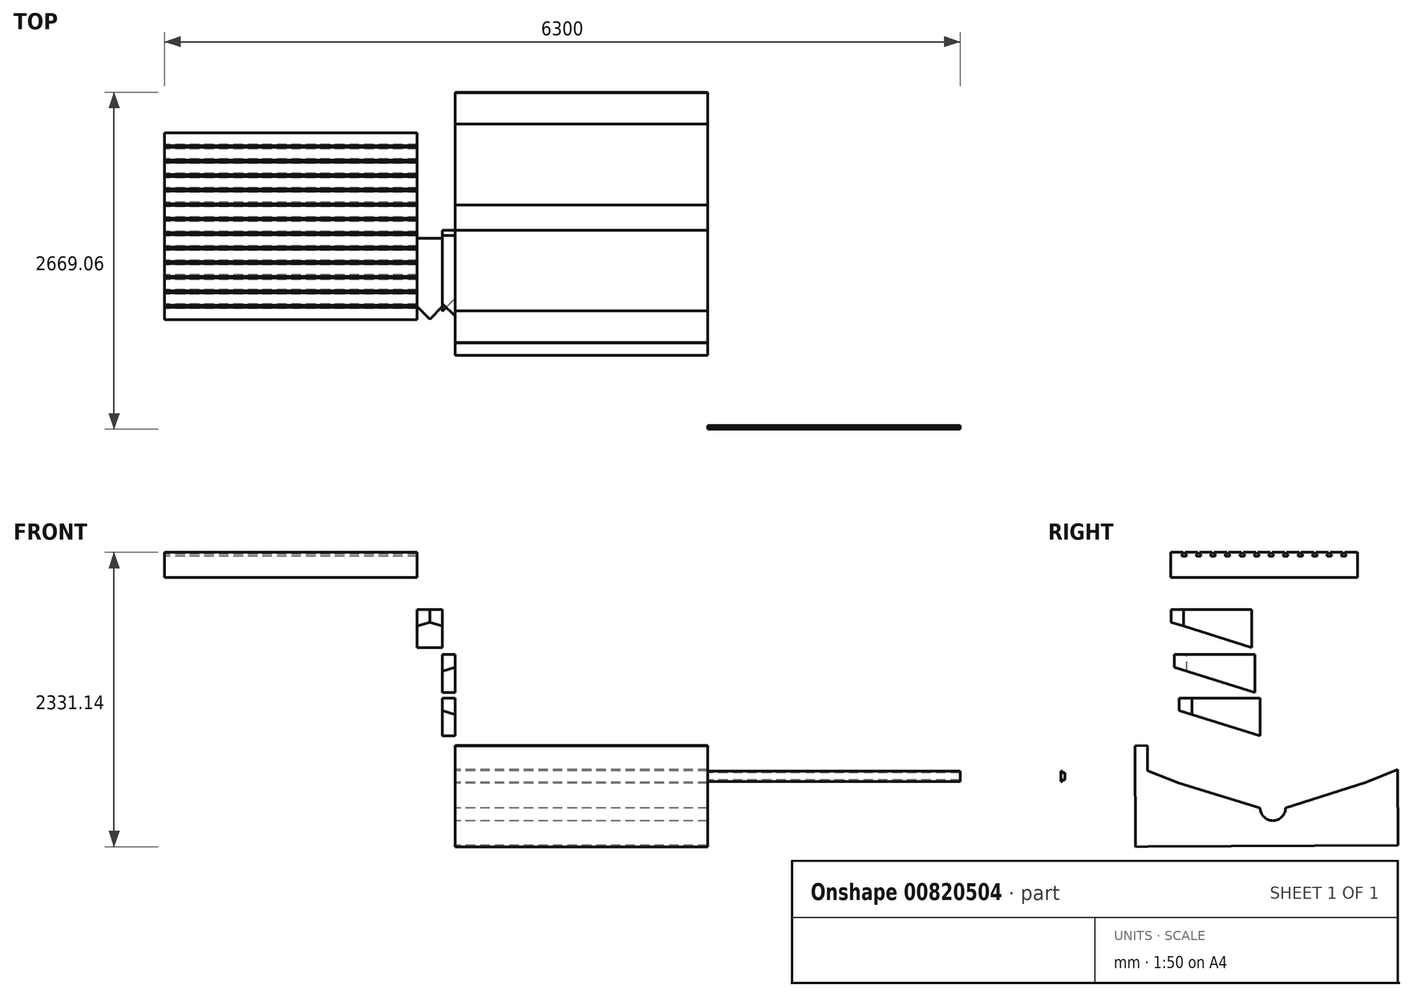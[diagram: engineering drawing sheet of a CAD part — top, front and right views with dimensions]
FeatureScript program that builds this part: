
annotation { "Feature Type Name" : "Feature", "Feature Type Description" : "" }
export const myFeature = defineFeature(function(context is Context, id is Id, definition is map)
    precondition{}
    {
        {
            var Q0;
            Q0=qCreatedBy(makeId("Right.planeOp"),FACE);
            var sketch = newSketch(context, id + "F0", { "sketchPlane" : qUnion([Q0])});
            skLineSegment(sketch, "E0", {"start": v(-68.68, 15) * mm, "end": v(31.32, 15) * mm});
            skLineSegment(sketch, "E1", {"start": v(31.32, 15) * mm, "end": v(31.32, 0) * mm});
            skLineSegment(sketch, "E2", {"start": v(31.32, 0) * mm, "end": v(21.32, 0) * mm});
            skLineSegment(sketch, "E3", {"start": v(21.32, 0) * mm, "end": v(21.32, -15) * mm});
            skLineSegment(sketch, "E4", {"start": v(21.32, -15) * mm, "end": v(56.32, -15) * mm});
            skLineSegment(sketch, "E5", {"start": v(56.32, -15) * mm, "end": v(56.32, 0) * mm});
            skLineSegment(sketch, "E6", {"start": v(56.32, 0) * mm, "end": v(46.32, 0) * mm});
            skLineSegment(sketch, "E7", {"start": v(46.32, 0) * mm, "end": v(46.32, 15) * mm});
            skLineSegment(sketch, "E8", {"start": v(46.32, 15) * mm, "end": v(146.32, 15) * mm});
            skLineSegment(sketch, "E9", {"start": v(146.32, 15) * mm, "end": v(146.32, 0) * mm});
            skLineSegment(sketch, "E10", {"start": v(146.32, 0) * mm, "end": v(136.32, 0) * mm});
            skLineSegment(sketch, "E11", {"start": v(136.32, 0) * mm, "end": v(136.32, -15) * mm});
            skLineSegment(sketch, "E12", {"start": v(136.32, -15) * mm, "end": v(171.32, -15) * mm});
            skLineSegment(sketch, "E13", {"start": v(171.32, -15) * mm, "end": v(171.32, 0) * mm});
            skLineSegment(sketch, "E14", {"start": v(171.32, 0) * mm, "end": v(161.32, 0) * mm});
            skLineSegment(sketch, "E15", {"start": v(161.32, 0) * mm, "end": v(161.32, 15) * mm});
            skLineSegment(sketch, "E16", {"start": v(161.32, 15) * mm, "end": v(261.32, 15) * mm});
            skLineSegment(sketch, "E17", {"start": v(261.32, 15) * mm, "end": v(261.32, 0) * mm});
            skLineSegment(sketch, "E18", {"start": v(261.32, 0) * mm, "end": v(251.32, 0) * mm});
            skLineSegment(sketch, "E19", {"start": v(251.32, 0) * mm, "end": v(251.32, -15) * mm});
            skLineSegment(sketch, "E20", {"start": v(251.32, -15) * mm, "end": v(286.32, -15) * mm});
            skLineSegment(sketch, "E21", {"start": v(286.32, -15) * mm, "end": v(286.32, 0) * mm});
            skLineSegment(sketch, "E22", {"start": v(286.32, 0) * mm, "end": v(276.32, 0) * mm});
            skLineSegment(sketch, "E23", {"start": v(276.32, 0) * mm, "end": v(276.32, 15) * mm});
            skLineSegment(sketch, "E24", {"start": v(276.32, 15) * mm, "end": v(376.32, 15) * mm});
            skLineSegment(sketch, "E25", {"start": v(376.32, 15) * mm, "end": v(376.32, 0) * mm});
            skLineSegment(sketch, "E26", {"start": v(376.32, 0) * mm, "end": v(366.32, 0) * mm});
            skLineSegment(sketch, "E27", {"start": v(366.32, 0) * mm, "end": v(366.32, -15) * mm});
            skLineSegment(sketch, "E28", {"start": v(366.32, -15) * mm, "end": v(401.32, -15) * mm});
            skLineSegment(sketch, "E29", {"start": v(401.32, -15) * mm, "end": v(401.32, 0) * mm});
            skLineSegment(sketch, "E30", {"start": v(401.32, 0) * mm, "end": v(391.32, 0) * mm});
            skLineSegment(sketch, "E31", {"start": v(391.32, 0) * mm, "end": v(391.32, 15) * mm});
            skLineSegment(sketch, "E32", {"start": v(391.32, 15) * mm, "end": v(491.32, 15) * mm});
            skLineSegment(sketch, "E33", {"start": v(491.32, 15) * mm, "end": v(491.32, 0) * mm});
            skLineSegment(sketch, "E34", {"start": v(491.32, 0) * mm, "end": v(481.32, 0) * mm});
            skLineSegment(sketch, "E35", {"start": v(481.32, 0) * mm, "end": v(481.32, -15) * mm});
            skLineSegment(sketch, "E36", {"start": v(481.32, -15) * mm, "end": v(516.32, -15) * mm});
            skLineSegment(sketch, "E37", {"start": v(516.32, -15) * mm, "end": v(516.32, 0) * mm});
            skLineSegment(sketch, "E38", {"start": v(516.32, 0) * mm, "end": v(506.32, 0) * mm});
            skLineSegment(sketch, "E39", {"start": v(506.32, 0) * mm, "end": v(506.32, 15) * mm});
            skLineSegment(sketch, "E40", {"start": v(506.32, 15) * mm, "end": v(606.32, 15) * mm});
            skLineSegment(sketch, "E41", {"start": v(606.32, 15) * mm, "end": v(606.32, 0) * mm});
            skLineSegment(sketch, "E42", {"start": v(606.32, 0) * mm, "end": v(596.32, 0) * mm});
            skLineSegment(sketch, "E43", {"start": v(596.32, 0) * mm, "end": v(596.32, -15) * mm});
            skLineSegment(sketch, "E44", {"start": v(596.32, -15) * mm, "end": v(631.32, -15) * mm});
            skLineSegment(sketch, "E45", {"start": v(631.32, -15) * mm, "end": v(631.32, 0) * mm});
            skLineSegment(sketch, "E46", {"start": v(631.32, 0) * mm, "end": v(621.32, 0) * mm});
            skLineSegment(sketch, "E47", {"start": v(621.32, 0) * mm, "end": v(621.32, 15) * mm});
            skLineSegment(sketch, "E48", {"start": v(621.32, 15) * mm, "end": v(721.32, 15) * mm});
            skLineSegment(sketch, "E49", {"start": v(721.32, 15) * mm, "end": v(721.32, 0) * mm});
            skLineSegment(sketch, "E50", {"start": v(721.32, 0) * mm, "end": v(711.32, 0) * mm});
            skLineSegment(sketch, "E51", {"start": v(711.32, 0) * mm, "end": v(711.32, -15) * mm});
            skLineSegment(sketch, "E52", {"start": v(711.32, -15) * mm, "end": v(746.32, -15) * mm});
            skLineSegment(sketch, "E53", {"start": v(746.32, -15) * mm, "end": v(746.32, 0) * mm});
            skLineSegment(sketch, "E54", {"start": v(746.32, 0) * mm, "end": v(736.32, 0) * mm});
            skLineSegment(sketch, "E55", {"start": v(736.32, 0) * mm, "end": v(736.32, 15) * mm});
            skLineSegment(sketch, "E56", {"start": v(736.32, 15) * mm, "end": v(836.32, 15) * mm});
            skLineSegment(sketch, "E57", {"start": v(836.32, 15) * mm, "end": v(836.32, 0) * mm});
            skLineSegment(sketch, "E58", {"start": v(836.32, 0) * mm, "end": v(826.32, 0) * mm});
            skLineSegment(sketch, "E59", {"start": v(826.32, 0) * mm, "end": v(826.32, -15) * mm});
            skLineSegment(sketch, "E60", {"start": v(826.32, -15) * mm, "end": v(861.32, -15) * mm});
            skLineSegment(sketch, "E61", {"start": v(861.32, -15) * mm, "end": v(861.32, 0) * mm});
            skLineSegment(sketch, "E62", {"start": v(861.32, 0) * mm, "end": v(851.32, 0) * mm});
            skLineSegment(sketch, "E63", {"start": v(851.32, 0) * mm, "end": v(851.32, 15) * mm});
            skLineSegment(sketch, "E64", {"start": v(851.32, 15) * mm, "end": v(951.32, 15) * mm});
            skLineSegment(sketch, "E65", {"start": v(951.32, 15) * mm, "end": v(951.32, 0) * mm});
            skLineSegment(sketch, "E66", {"start": v(951.32, 0) * mm, "end": v(941.32, 0) * mm});
            skLineSegment(sketch, "E67", {"start": v(941.32, 0) * mm, "end": v(941.32, -15) * mm});
            skLineSegment(sketch, "E68", {"start": v(941.32, -15) * mm, "end": v(976.32, -15) * mm});
            skLineSegment(sketch, "E69", {"start": v(976.32, -15) * mm, "end": v(976.32, 0) * mm});
            skLineSegment(sketch, "E70", {"start": v(976.32, 0) * mm, "end": v(966.32, 0) * mm});
            skLineSegment(sketch, "E71", {"start": v(966.32, 0) * mm, "end": v(966.32, 15) * mm});
            skLineSegment(sketch, "E72", {"start": v(966.32, 15) * mm, "end": v(1066.32, 15) * mm});
            skLineSegment(sketch, "E73", {"start": v(1066.32, 15) * mm, "end": v(1066.32, 0) * mm});
            skLineSegment(sketch, "E74", {"start": v(1066.32, 0) * mm, "end": v(1056.32, 0) * mm});
            skLineSegment(sketch, "E75", {"start": v(1056.32, 0) * mm, "end": v(1056.32, -15) * mm});
            skLineSegment(sketch, "E76", {"start": v(1056.32, -15) * mm, "end": v(1091.32, -15) * mm});
            skLineSegment(sketch, "E77", {"start": v(1091.32, -15) * mm, "end": v(1091.32, 0) * mm});
            skLineSegment(sketch, "E78", {"start": v(1091.32, 0) * mm, "end": v(1081.32, 0) * mm});
            skLineSegment(sketch, "E79", {"start": v(1081.32, 0) * mm, "end": v(1081.32, 15) * mm});
            skLineSegment(sketch, "E80", {"start": v(1081.32, 15) * mm, "end": v(1181.32, 15) * mm});
            skLineSegment(sketch, "E81", {"start": v(1181.32, 15) * mm, "end": v(1181.32, 0) * mm});
            skLineSegment(sketch, "E82", {"start": v(1181.32, 0) * mm, "end": v(1171.32, 0) * mm});
            skLineSegment(sketch, "E83", {"start": v(1171.32, 0) * mm, "end": v(1171.32, -15) * mm});
            skLineSegment(sketch, "E84", {"start": v(1171.32, -15) * mm, "end": v(1206.32, -15) * mm});
            skLineSegment(sketch, "E85", {"start": v(1206.32, -15) * mm, "end": v(1206.32, 0) * mm});
            skLineSegment(sketch, "E86", {"start": v(1206.32, 0) * mm, "end": v(1196.32, 0) * mm});
            skLineSegment(sketch, "E87", {"start": v(1196.32, 0) * mm, "end": v(1196.32, 15) * mm});
            skLineSegment(sketch, "E88", {"start": v(1196.32, 15) * mm, "end": v(1296.32, 15) * mm});
            skPoint(sketch, "E88.endSnap0", {"position": v(1131.32, 15) * mm});
            skLineSegment(sketch, "E89", {"start": v(1296.32, 15) * mm, "end": v(1296.32, 0) * mm});
            skLineSegment(sketch, "E90", {"start": v(1296.32, 0) * mm, "end": v(1286.32, 0) * mm});
            skLineSegment(sketch, "E91", {"start": v(1286.32, 0) * mm, "end": v(1286.32, -15) * mm});
            skLineSegment(sketch, "E92", {"start": v(1286.32, -15) * mm, "end": v(1321.32, -15) * mm});
            skLineSegment(sketch, "E93", {"start": v(1321.32, -15) * mm, "end": v(1321.32, 0) * mm});
            skLineSegment(sketch, "E94", {"start": v(1321.32, 0) * mm, "end": v(1311.32, 0) * mm});
            skLineSegment(sketch, "E95", {"start": v(1311.32, 0) * mm, "end": v(1311.32, 15) * mm});
            skLineSegment(sketch, "E96", {"start": v(1311.32, 15) * mm, "end": v(1411.32, 15) * mm});
            skLineSegment(sketch, "E97", {"start": v(1411.32, 15) * mm, "end": v(1411.32, -185) * mm});
            skLineSegment(sketch, "E98", {"start": v(1411.32, -185) * mm, "end": v(-68.68, -185) * mm});
            skLineSegment(sketch, "E99", {"start": v(-68.68, -185) * mm, "end": v(-68.68, 15) * mm});
            skSolve(sketch);
        }
        {
            var Q0;
            Q0=makeQuery(id+"F0.imprint","IMPRINT",FACE,{"disambiguationData":[TD([[makeQuery(id+"F0.imprint","IMPRINT",EDGE,{"derivedFrom":sQuery(id+"F0.wireOp",EDGE,"E0")}),-1.0]])]});
            extrude(context, id + "F1", {"entities" : qUnion([Q0]), "depth" : 2000 * mm, "offsetDistance" : 25 * mm});
        }
        {
            var Q0;
            Q0=makeQuery(id+"F1.opExtrude","CAP_FACE",FACE,{"disambiguationData":[OSD([sQuery(id+"F0.wireOp",EDGE,"E0"),sQuery(id+"F0.wireOp",EDGE,"E1"),sQuery(id+"F0.wireOp",EDGE,"E2"),sQuery(id+"F0.wireOp",EDGE,"E3"),sQuery(id+"F0.wireOp",EDGE,"E4"),sQuery(id+"F0.wireOp",EDGE,"E5"),sQuery(id+"F0.wireOp",EDGE,"E6"),sQuery(id+"F0.wireOp",EDGE,"E7"),sQuery(id+"F0.wireOp",EDGE,"E8"),sQuery(id+"F0.wireOp",EDGE,"E9"),sQuery(id+"F0.wireOp",EDGE,"E10"),sQuery(id+"F0.wireOp",EDGE,"E11"),sQuery(id+"F0.wireOp",EDGE,"E12"),sQuery(id+"F0.wireOp",EDGE,"E13"),sQuery(id+"F0.wireOp",EDGE,"E14"),sQuery(id+"F0.wireOp",EDGE,"E15"),sQuery(id+"F0.wireOp",EDGE,"E16"),sQuery(id+"F0.wireOp",EDGE,"E17"),sQuery(id+"F0.wireOp",EDGE,"E18"),sQuery(id+"F0.wireOp",EDGE,"E19"),sQuery(id+"F0.wireOp",EDGE,"E20"),sQuery(id+"F0.wireOp",EDGE,"E21"),sQuery(id+"F0.wireOp",EDGE,"E22"),sQuery(id+"F0.wireOp",EDGE,"E23"),sQuery(id+"F0.wireOp",EDGE,"E24"),sQuery(id+"F0.wireOp",EDGE,"E25"),sQuery(id+"F0.wireOp",EDGE,"E26"),sQuery(id+"F0.wireOp",EDGE,"E27"),sQuery(id+"F0.wireOp",EDGE,"E28"),sQuery(id+"F0.wireOp",EDGE,"E29"),sQuery(id+"F0.wireOp",EDGE,"E30"),sQuery(id+"F0.wireOp",EDGE,"E31"),sQuery(id+"F0.wireOp",EDGE,"E32"),sQuery(id+"F0.wireOp",EDGE,"E33"),sQuery(id+"F0.wireOp",EDGE,"E34"),sQuery(id+"F0.wireOp",EDGE,"E35"),sQuery(id+"F0.wireOp",EDGE,"E36"),sQuery(id+"F0.wireOp",EDGE,"E37"),sQuery(id+"F0.wireOp",EDGE,"E38"),sQuery(id+"F0.wireOp",EDGE,"E39"),sQuery(id+"F0.wireOp",EDGE,"E40"),sQuery(id+"F0.wireOp",EDGE,"E41"),sQuery(id+"F0.wireOp",EDGE,"E42"),sQuery(id+"F0.wireOp",EDGE,"E43"),sQuery(id+"F0.wireOp",EDGE,"E44"),sQuery(id+"F0.wireOp",EDGE,"E45"),sQuery(id+"F0.wireOp",EDGE,"E46"),sQuery(id+"F0.wireOp",EDGE,"E47"),sQuery(id+"F0.wireOp",EDGE,"E48"),sQuery(id+"F0.wireOp",EDGE,"E49"),sQuery(id+"F0.wireOp",EDGE,"E50"),sQuery(id+"F0.wireOp",EDGE,"E51"),sQuery(id+"F0.wireOp",EDGE,"E52"),sQuery(id+"F0.wireOp",EDGE,"E53"),sQuery(id+"F0.wireOp",EDGE,"E54"),sQuery(id+"F0.wireOp",EDGE,"E55"),sQuery(id+"F0.wireOp",EDGE,"E56"),sQuery(id+"F0.wireOp",EDGE,"E57"),sQuery(id+"F0.wireOp",EDGE,"E58"),sQuery(id+"F0.wireOp",EDGE,"E59"),sQuery(id+"F0.wireOp",EDGE,"E60"),sQuery(id+"F0.wireOp",EDGE,"E61"),sQuery(id+"F0.wireOp",EDGE,"E62"),sQuery(id+"F0.wireOp",EDGE,"E63"),sQuery(id+"F0.wireOp",EDGE,"E64"),sQuery(id+"F0.wireOp",EDGE,"E65"),sQuery(id+"F0.wireOp",EDGE,"E66"),sQuery(id+"F0.wireOp",EDGE,"E67"),sQuery(id+"F0.wireOp",EDGE,"E68"),sQuery(id+"F0.wireOp",EDGE,"E69"),sQuery(id+"F0.wireOp",EDGE,"E70"),sQuery(id+"F0.wireOp",EDGE,"E71"),sQuery(id+"F0.wireOp",EDGE,"E72"),sQuery(id+"F0.wireOp",EDGE,"E73"),sQuery(id+"F0.wireOp",EDGE,"E74"),sQuery(id+"F0.wireOp",EDGE,"E75"),sQuery(id+"F0.wireOp",EDGE,"E76"),sQuery(id+"F0.wireOp",EDGE,"E77"),sQuery(id+"F0.wireOp",EDGE,"E78"),sQuery(id+"F0.wireOp",EDGE,"E79"),sQuery(id+"F0.wireOp",EDGE,"E80"),sQuery(id+"F0.wireOp",EDGE,"E81"),sQuery(id+"F0.wireOp",EDGE,"E82"),sQuery(id+"F0.wireOp",EDGE,"E83"),sQuery(id+"F0.wireOp",EDGE,"E84"),sQuery(id+"F0.wireOp",EDGE,"E85"),sQuery(id+"F0.wireOp",EDGE,"E86"),sQuery(id+"F0.wireOp",EDGE,"E87"),sQuery(id+"F0.wireOp",EDGE,"E88"),sQuery(id+"F0.wireOp",EDGE,"E89"),sQuery(id+"F0.wireOp",EDGE,"E90"),sQuery(id+"F0.wireOp",EDGE,"E91"),sQuery(id+"F0.wireOp",EDGE,"E92"),sQuery(id+"F0.wireOp",EDGE,"E93"),sQuery(id+"F0.wireOp",EDGE,"E94"),sQuery(id+"F0.wireOp",EDGE,"E95"),sQuery(id+"F0.wireOp",EDGE,"E96"),sQuery(id+"F0.wireOp",EDGE,"E97"),sQuery(id+"F0.wireOp",EDGE,"E98"),sQuery(id+"F0.wireOp",EDGE,"E99")])],"isStart":false});
            var sketch = newSketch(context, id + "F2", { "sketchPlane" : qUnion([Q0])});
            skLineSegment(sketch, "E100", {"start": v(-64.04, -438.2) * mm, "end": v(575.96, -438.2) * mm});
            skLineSegment(sketch, "E101", {"start": v(575.96, -438.2) * mm, "end": v(575.96, -738.2) * mm});
            skLineSegment(sketch, "E102", {"start": v(-64.04, -438.2) * mm, "end": v(-64.04, -538.2) * mm});
            skLineSegment(sketch, "E103", {"start": v(-64.04, -538.2) * mm, "end": v(575.96, -738.2) * mm});
            skSolve(sketch);
        }
        {
            var Q0;
            Q0=makeQuery(id+"F2.imprint","IMPRINT",FACE,{"disambiguationData":[TD([[makeQuery(id+"F2.imprint","IMPRINT",EDGE,{"derivedFrom":sQuery(id+"F2.wireOp",EDGE,"E100")}),-1.0]])]});
            extrude(context, id + "F3", {"entities" : qUnion([Q0]), "depth" : 200 * mm, "offsetDistance" : 25 * mm});
        }
        {
            var Q0;
            Q0=makeQuery(id+"F3.opExtrude","CAP_EDGE",EDGE,{"disambiguationData":[OSD([sQuery(id+"F2.wireOp",EDGE,"E102")])],"isStart":false});
            chamfer(context, id + "F4", {"entities" : qUnion([Q0]), "width" : 100 * mm, "tangentPropagation" : true});
        }
        {
            var Q0;
            Q0=makeQuery(id+"F3.opExtrude","CAP_EDGE",EDGE,{"disambiguationData":[OSD([sQuery(id+"F2.wireOp",EDGE,"E102")])],"isStart":true});
            chamfer(context, id + "F5", {"entities" : qUnion([Q0]), "width" : 100 * mm, "tangentPropagation" : true});
        }
        {
            var Q0;
            Q0=makeQuery(id+"F3.opExtrude","CAP_FACE",FACE,{"disambiguationData":[OSD([sQuery(id+"F2.wireOp",EDGE,"E100"),sQuery(id+"F2.wireOp",EDGE,"E101"),sQuery(id+"F2.wireOp",EDGE,"E102"),sQuery(id+"F2.wireOp",EDGE,"E103")])],"isStart":false});
            var sketch = newSketch(context, id + "F6", { "sketchPlane" : qUnion([Q0])});
            skLineSegment(sketch, "E104", {"start": v(600.58, -794.53) * mm, "end": v(-39.42, -794.53) * mm});
            skLineSegment(sketch, "E105", {"start": v(600.58, -794.53) * mm, "end": v(600.58, -1094.53) * mm});
            skLineSegment(sketch, "E106", {"start": v(-39.42, -794.53) * mm, "end": v(-39.42, -894.53) * mm});
            skLineSegment(sketch, "E107", {"start": v(-39.42, -894.53) * mm, "end": v(600.58, -1094.53) * mm});
            skSolve(sketch);
        }
        {
            var Q0;
            Q0=makeQuery(id+"F6.imprint","IMPRINT",FACE,{"disambiguationData":[TD([[makeQuery(id+"F6.imprint","IMPRINT",EDGE,{"derivedFrom":sQuery(id+"F6.wireOp",EDGE,"E104")}),1.0]])]});
            var sketch = newSketch(context, id + "F7", { "sketchPlane" : qUnion([Q0])});
            skLineSegment(sketch, "E108", {"start": v(640, -1138.8) * mm, "end": v(0, -1138.8) * mm});
            skLineSegment(sketch, "E109", {"start": v(0, -1138.8) * mm, "end": v(0, -1238.8) * mm});
            skLineSegment(sketch, "E110", {"start": v(640, -1138.8) * mm, "end": v(640, -1438.8) * mm});
            skLineSegment(sketch, "E111", {"start": v(640, -1438.8) * mm, "end": v(0, -1238.8) * mm});
            skSolve(sketch);
        }
        {
            var Q0;
            Q0=makeQuery(id+"F6.imprint","IMPRINT",FACE,{"disambiguationData":[TD([[makeQuery(id+"F6.imprint","IMPRINT",EDGE,{"derivedFrom":sQuery(id+"F6.wireOp",EDGE,"E104")}),1.0]])]});
            extrude(context, id + "F8", {"entities" : qUnion([Q0]), "depth" : 100 * mm, "offsetDistance" : 25 * mm});
        }
        {
            var Q0;
            Q0=makeQuery(id+"F7.imprint","IMPRINT",FACE,{"disambiguationData":[TD([[makeQuery(id+"F7.imprint","IMPRINT",EDGE,{"derivedFrom":sQuery(id+"F7.wireOp",EDGE,"E108")}),1.0]])]});
            extrude(context, id + "F9", {"entities" : qUnion([Q0]), "depth" : 100 * mm, "offsetDistance" : 25 * mm});
        }
        {
            var Q0;
            Q0=makeQuery(id+"F8.opExtrude","CAP_EDGE",EDGE,{"disambiguationData":[OSD([sQuery(id+"F6.wireOp",EDGE,"E106")])],"isStart":true});
            chamfer(context, id + "F10", {"entities" : qUnion([Q0]), "width" : 100 * mm, "tangentPropagation" : true});
        }
        {
            var Q0;
            Q0=makeQuery(id+"F9.opExtrude","CAP_EDGE",EDGE,{"disambiguationData":[OSD([sQuery(id+"F7.wireOp",EDGE,"E109")])],"isStart":false});
            chamfer(context, id + "F11", {"entities" : qUnion([Q0]), "width" : 100 * mm, "tangentPropagation" : true});
        }
        {
            var Q0;
            Q0=makeQuery(id+"F9.opExtrude","CAP_FACE",FACE,{"disambiguationData":[OSD([sQuery(id+"F7.wireOp",EDGE,"E108"),sQuery(id+"F7.wireOp",EDGE,"E109"),sQuery(id+"F7.wireOp",EDGE,"E110"),sQuery(id+"F7.wireOp",EDGE,"E111")])],"isStart":false});
            var sketch = newSketch(context, id + "F12", { "sketchPlane" : qUnion([Q0])});
            skArc(sketch, "E112", {"start": v(641.8, -2010.2) * mm, "mid": v(741.8, -2109.6) * mm, "end": v(841.79, -2010.2) * mm});
            skLineSegment(sketch, "E113", {"start": v(641.8, -2010.2) * mm, "end": v(0.6, -1814.05) * mm});
            skLineSegment(sketch, "E114", {"start": v(841.79, -2010.2) * mm, "end": v(1480.57, -1806.35) * mm});
            skLineSegment(sketch, "E115", {"start": v(1480.57, -1806.35) * mm, "end": v(1729.97, -1704.85) * mm});
            skLineSegment(sketch, "E116", {"start": v(0.6, -1814.05) * mm, "end": v(-250, -1715.55) * mm});
            skLineSegment(sketch, "E117", {"start": v(1729.97, -1704.85) * mm, "end": v(1733.58, -2304.83) * mm});
            skLineSegment(sketch, "E118", {"start": v(1733.58, -2304.83) * mm, "end": v(-246.39, -2315.54) * mm});
            skLineSegment(sketch, "E119", {"start": v(-250, -1715.55) * mm, "end": v(-251.2, -1515.56) * mm});
            skLineSegment(sketch, "E120", {"start": v(-251.2, -1515.56) * mm, "end": v(-351.2, -1516.16) * mm});
            skLineSegment(sketch, "E121", {"start": v(-351.2, -1516.16) * mm, "end": v(-346.38, -2316.14) * mm});
            skLineSegment(sketch, "E122", {"start": v(-346.38, -2316.14) * mm, "end": v(-246.39, -2315.54) * mm});
            skSolve(sketch);
        }
        {
            var Q0;
            Q0=makeQuery(id+"F12.imprint","IMPRINT",FACE,{"disambiguationData":[TD([[makeQuery(id+"F12.imprint","IMPRINT",EDGE,{"derivedFrom":sQuery(id+"F12.wireOp",EDGE,"E112")}),-1.0]])]});
            extrude(context, id + "F13", {"entities" : qUnion([Q0]), "depth" : 2000 * mm, "offsetDistance" : 25 * mm});
        }
        {
            var Q0;
            Q0=makeQuery(id+"F13.opExtrude","CAP_FACE",FACE,{"disambiguationData":[OSD([sQuery(id+"F12.wireOp",EDGE,"E112"),sQuery(id+"F12.wireOp",EDGE,"E113"),sQuery(id+"F12.wireOp",EDGE,"E114"),sQuery(id+"F12.wireOp",EDGE,"E115"),sQuery(id+"F12.wireOp",EDGE,"E116"),sQuery(id+"F12.wireOp",EDGE,"E117"),sQuery(id+"F12.wireOp",EDGE,"E118"),sQuery(id+"F12.wireOp",EDGE,"E119"),sQuery(id+"F12.wireOp",EDGE,"E120"),sQuery(id+"F12.wireOp",EDGE,"E121"),sQuery(id+"F12.wireOp",EDGE,"E122")])],"isStart":false});
            var sketch = newSketch(context, id + "F14", { "sketchPlane" : qUnion([Q0])});
            skLineSegment(sketch, "E123", {"start": v(-935.48, -1718.7) * mm, "end": v(-935.48, -1798.7) * mm});
            skLineSegment(sketch, "E124", {"start": v(-935.48, -1798.7) * mm, "end": v(-925.48, -1798.7) * mm});
            skLineSegment(sketch, "E125", {"start": v(-925.48, -1798.7) * mm, "end": v(-925.48, -1788.7) * mm});
            skLineSegment(sketch, "E126", {"start": v(-925.48, -1788.7) * mm, "end": v(-905.48, -1788.7) * mm});
            skLineSegment(sketch, "E127", {"start": v(-905.48, -1788.7) * mm, "end": v(-905.48, -1728.7) * mm});
            skLineSegment(sketch, "E128", {"start": v(-905.48, -1728.7) * mm, "end": v(-925.48, -1728.7) * mm});
            skLineSegment(sketch, "E129", {"start": v(-925.48, -1728.7) * mm, "end": v(-925.48, -1718.7) * mm});
            skLineSegment(sketch, "E130", {"start": v(-925.48, -1718.7) * mm, "end": v(-935.48, -1718.7) * mm});
            skSolve(sketch);
        }
        {
            var Q0;
            Q0=makeQuery(id+"F14.imprint","IMPRINT",FACE,{"disambiguationData":[TD([[makeQuery(id+"F14.imprint","IMPRINT",EDGE,{"derivedFrom":sQuery(id+"F14.wireOp",EDGE,"E123")}),1.0]])]});
            extrude(context, id + "F15", {"entities" : qUnion([Q0]), "depth" : 2000 * mm, "offsetDistance" : 25 * mm});
        }
    });
